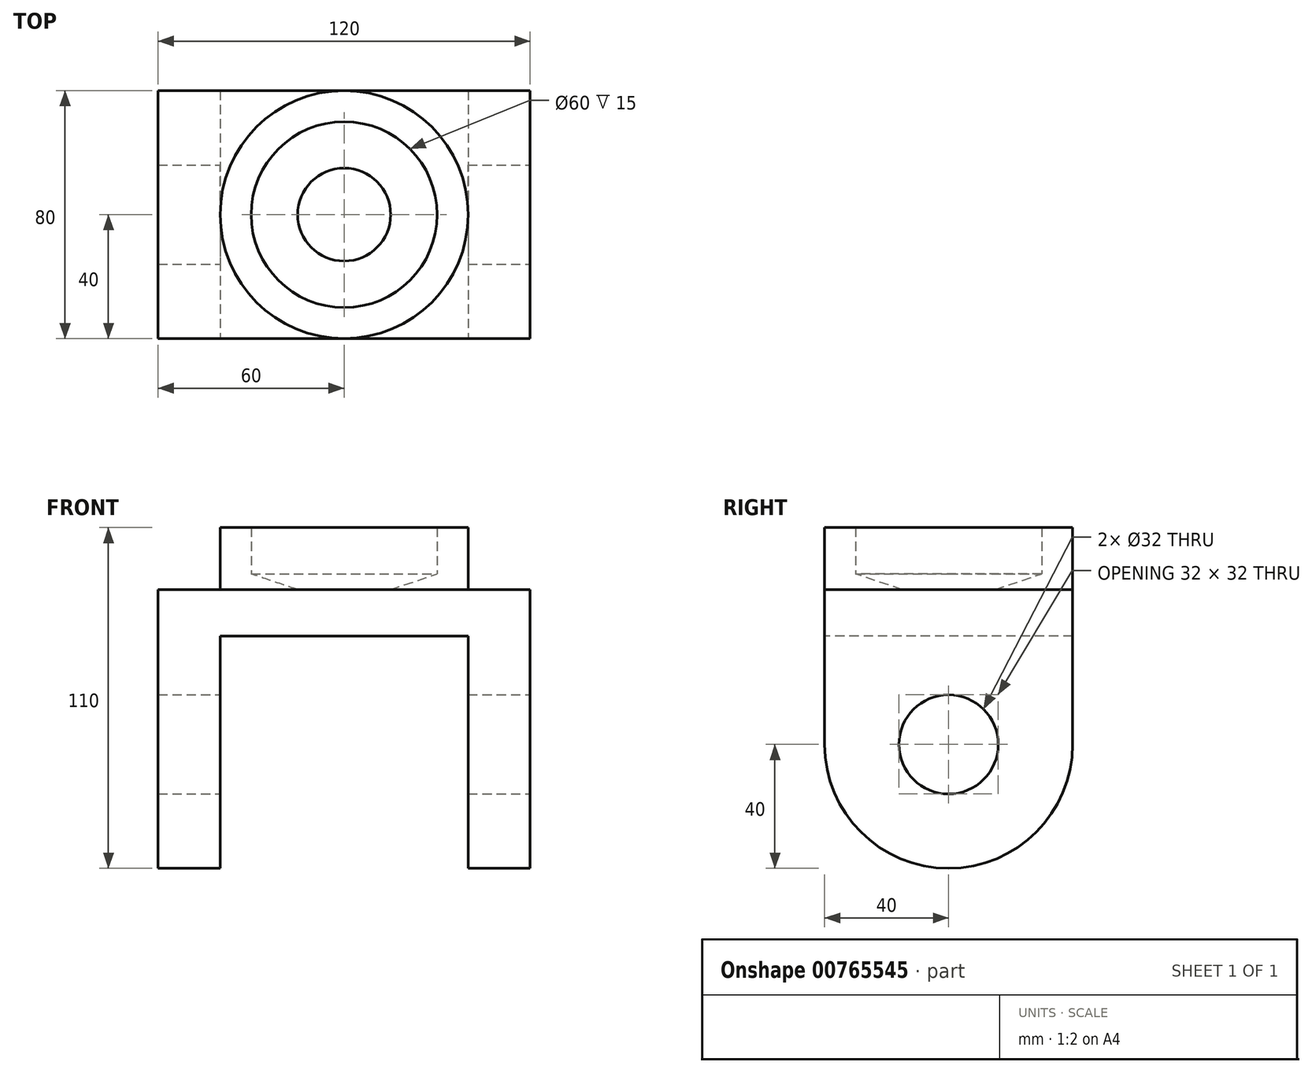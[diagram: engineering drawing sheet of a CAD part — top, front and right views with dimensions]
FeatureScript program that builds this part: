
annotation { "Feature Type Name" : "Feature", "Feature Type Description" : "" }
export const myFeature = defineFeature(function(context is Context, id is Id, definition is map)
    precondition{}
    {
        {
            var Q0;
            Q0=qCreatedBy(makeId("Top.planeOp"),FACE);
            var sketch = newSketch(context, id + "F0", { "sketchPlane" : qUnion([Q0])});
            skLineSegment(sketch, "E0.bottom", {"start": v(60, -40) * mm, "end": v(-60, -40) * mm});
            skLineSegment(sketch, "E0.top", {"start": v(60, 40) * mm, "end": v(-60, 40) * mm});
            skLineSegment(sketch, "E0.left", {"start": v(60, -40) * mm, "end": v(60, 40) * mm});
            skLineSegment(sketch, "E0.right", {"start": v(-60, -40) * mm, "end": v(-60, 40) * mm});
            skPoint(sketch, "E0.middle", {"position": v(0, 0) * mm});
            skCircle(sketch, "E1", {"center": v(0, 0) * mm, "radius": 40 * mm});
            skCircle(sketch, "E2", {"center": v(0, 0) * mm, "radius": 30 * mm});
            skCircle(sketch, "E3", {"center": v(0, 0) * mm, "radius": 15 * mm});
            skSolve(sketch);
        }
        {
            var Q0;
            Q0 = qSketchRegion(id + "F0", true);
            var Q1;
            Q1=makeQuery(id+"F0.imprint","IMPRINT",FACE,{"disambiguationData":[TD([[makeQuery(id+"F0.imprint","IMPRINT",EDGE,{"derivedFrom":sQuery(id+"F0.wireOp",EDGE,"E2")}),1.0]])]});
            var Q2;
            Q2=makeQuery(id+"F0.imprint","IMPRINT",FACE,{"disambiguationData":[TD([[makeQuery(id+"F0.imprint","IMPRINT",EDGE,{"derivedFrom":sQuery(id+"F0.wireOp",EDGE,"E3")}),1.0]])]});
            var Q3;
            Q3 = qSketchRegion(id + "F2", true);
            extrude(context, id + "F1", {"entities" : qUnion([Q0, Q1, Q2, Q3]), "depth" : -90 * mm, "offsetDistance" : 25 * mm});
        }
        {
            var Q0;
            Q0=makeQuery(id+"F1.opExtrude","SWEPT_FACE",FACE,{"disambiguationData":[OSD([sQuery(id+"F0.wireOp",EDGE,"E0.left")])]});
            var sketch = newSketch(context, id + "F2", { "sketchPlane" : qUnion([Q0])});
            skCircle(sketch, "E4", {"center": v(0, -50) * mm, "radius": 16 * mm});
            skCircle(sketch, "E5", {"center": v(0, -50) * mm, "radius": 40 * mm});
            skSolve(sketch);
        }
        {
            var Q0;
            {var subQ0=sQuery(id+"F2.wireOp",EDGE,"E5");var subQ1=sQuery(id+"F0.wireOp",EDGE,"E0.left");var subQ4=makeQuery(id+"F1.opExtrude","CAP_EDGE",EDGE,{"disambiguationData":[OSD([subQ1])],"isStart":false});var subQ5=makeQuery(id+"F2.imprint","INTERSECT",VERTEX,{"derivedFrom":[subQ4,subQ0]});Q0=makeQuery(id+"F2.imprint","IMPRINT",FACE,{"disambiguationData":[TD([[makeQuery(id+"F2.imprint","IMPRINT",EDGE,{"disambiguationData":[TD([[subQ5,1.0]])],"derivedFrom":subQ0}),-1.0]])]});}
            var Q1;
            {var subQ0=sQuery(id+"F2.wireOp",EDGE,"E5");var subQ1=sQuery(id+"F0.wireOp",EDGE,"E0.left");var subQ4=makeQuery(id+"F1.opExtrude","CAP_EDGE",EDGE,{"disambiguationData":[OSD([subQ1])],"isStart":false});var subQ5=makeQuery(id+"F2.imprint","INTERSECT",VERTEX,{"derivedFrom":[subQ4,subQ0]});Q1=makeQuery(id+"F2.imprint","IMPRINT",FACE,{"disambiguationData":[TD([[makeQuery(id+"F2.imprint","IMPRINT",EDGE,{"disambiguationData":[TD([[subQ5,-1.0]])],"derivedFrom":subQ0}),-1.0]])]});}
            var Q2;
            Q2=makeQuery(id+"F2.imprint","IMPRINT",FACE,{"disambiguationData":[TD([[makeQuery(id+"F2.imprint","IMPRINT",EDGE,{"derivedFrom":sQuery(id+"F2.wireOp",EDGE,"E4")}),1.0]])]});
            extrude(context, id + "F3", {"entities" : qUnion([Q0, Q1, Q2]), "operationType" : NewBodyOperationType.REMOVE, "oppositeDirection" : true, "depth" : 250 * mm, "offsetDistance" : 25 * mm});
        }
        {
            var Q0;
            Q0=makeQuery(id+"F2.imprint","IMPRINT",FACE,{"disambiguationData":[TD([[makeQuery(id+"F2.imprint","IMPRINT",EDGE,{"derivedFrom":sQuery(id+"F2.wireOp",EDGE,"E4")}),1.0]])]});
            extrude(context, id + "F4", {"entities" : qUnion([Q0]), "operationType" : NewBodyOperationType.REMOVE, "oppositeDirection" : true, "depth" : 250 * mm, "offsetDistance" : 25 * mm});
        }
        {
            var Q0;
            Q0=makeQuery(id+"F2.imprint","IMPRINT",FACE,{"disambiguationData":[TD([[makeQuery(id+"F2.imprint","IMPRINT",EDGE,{"derivedFrom":sQuery(id+"F2.wireOp",EDGE,"E4")}),1.0]])]});
            extrude(context, id + "F5", {"entities" : qUnion([Q0]), "operationType" : NewBodyOperationType.REMOVE, "oppositeDirection" : true, "depth" : 250 * mm, "offsetDistance" : 25 * mm});
        }
        {
            var Q0;
            Q0=makeQuery(id+"F1.opExtrude","SWEPT_FACE",FACE,{"disambiguationData":[OSD([sQuery(id+"F0.wireOp",EDGE,"E0.bottom")])]});
            var sketch = newSketch(context, id + "F6", { "sketchPlane" : qUnion([Q0])});
            skLineSegment(sketch, "E6.bottom", {"start": v(-40, -15) * mm, "end": v(40, -15) * mm});
            skLineSegment(sketch, "E6.top", {"start": v(-40, -90) * mm, "end": v(40, -90) * mm});
            skLineSegment(sketch, "E6.left", {"start": v(-40, -15) * mm, "end": v(-40, -90) * mm});
            skLineSegment(sketch, "E6.right", {"start": v(40, -15) * mm, "end": v(40, -90) * mm});
            skSolve(sketch);
        }
        {
            var Q0;
            {var subQ0=sQuery(id+"F6.wireOp",EDGE,"E6.top");Q0=makeQuery(id+"F6.imprint","IMPRINT",FACE,{"disambiguationData":[TD([[makeQuery(id+"F6.imprint","IMPRINT",EDGE,{"derivedFrom":subQ0}),1.0]])]});}
            var Q1;
            {var subQ0=sQuery(id+"F6.wireOp",EDGE,"E6.bottom");Q1=makeQuery(id+"F6.imprint","IMPRINT",FACE,{"disambiguationData":[TD([[makeQuery(id+"F6.imprint","IMPRINT",EDGE,{"derivedFrom":subQ0}),-1.0]])]});}
            extrude(context, id + "F7", {"entities" : qUnion([Q0, Q1]), "operationType" : NewBodyOperationType.REMOVE, "oppositeDirection" : true, "depth" : 250 * mm, "offsetDistance" : 25 * mm});
        }
        {
            var Q0;
            {var subQ0=sQuery(id+"F2.wireOp",EDGE,"E5");var subQ1=sQuery(id+"F0.wireOp",EDGE,"E0.left");var subQ4=makeQuery(id+"F1.opExtrude","CAP_EDGE",EDGE,{"disambiguationData":[OSD([subQ1])],"isStart":false});var subQ5=makeQuery(id+"F2.imprint","INTERSECT",VERTEX,{"derivedFrom":[subQ4,subQ0]});Q0=makeQuery(id+"F2.imprint","IMPRINT",FACE,{"disambiguationData":[TD([[makeQuery(id+"F2.imprint","IMPRINT",EDGE,{"disambiguationData":[TD([[subQ5,1.0]])],"derivedFrom":subQ0}),-1.0]])]});}
            extrude(context, id + "F8", {"entities" : qUnion([Q0]), "operationType" : NewBodyOperationType.REMOVE, "oppositeDirection" : true, "depth" : 25 * mm, "offsetDistance" : 25 * mm});
        }
        {
            var Q0;
            Q0=qCreatedBy(makeId("Front.planeOp"),FACE);
            var sketch = newSketch(context, id + "F9", { "sketchPlane" : qUnion([Q0])});
            skLineSegment(sketch, "E7", {"start": v(-40, 0) * mm, "end": v(-40, 20) * mm});
            skLineSegment(sketch, "E8", {"start": v(-40, 20) * mm, "end": v(-30, 20) * mm});
            skLineSegment(sketch, "E9", {"start": v(-30, 20) * mm, "end": v(-30, 5) * mm});
            skLineSegment(sketch, "E10", {"start": v(-30, 5) * mm, "end": v(-15, 0) * mm});
            skLineSegment(sketch, "E11", {"start": v(0, 0) * mm, "end": v(0, 43.53) * mm});
            skLineSegment(sketch, "E12", {"start": v(-15, 0) * mm, "end": v(-40, 0) * mm});
            skSolve(sketch);
        }
        {
            var Q0;
            Q0=makeQuery(id+"F9.imprint","IMPRINT",FACE,{"disambiguationData":[TD([[makeQuery(id+"F9.imprint","IMPRINT",EDGE,{"derivedFrom":sQuery(id+"F9.wireOp",EDGE,"E7")}),-1.0]])]});
            var Q1;
            Q1=sQuery(id+"F9.wireOp",EDGE,"E7");
            var Q2;
            Q2=sQuery(id+"F9.wireOp",EDGE,"E9");
            var Q3;
            Q3=sQuery(id+"F9.wireOp",EDGE,"E10");
            var Q4;
            Q4=sQuery(id+"F9.wireOp",EDGE,"E8");
            var Q5;
            Q5=sQuery(id+"F9.wireOp",EDGE,"E11");
            revolve(context, id + "F10", {"surfaceOperationType" : NewSurfaceOperationType.NEW, "entities" : qUnion([Q0]), "surfaceEntities" : qUnion([Q1, Q2, Q3, Q4]), "axis" : qUnion([Q5]), "revolveType" : RevolveType.FULL});
        }
    });
